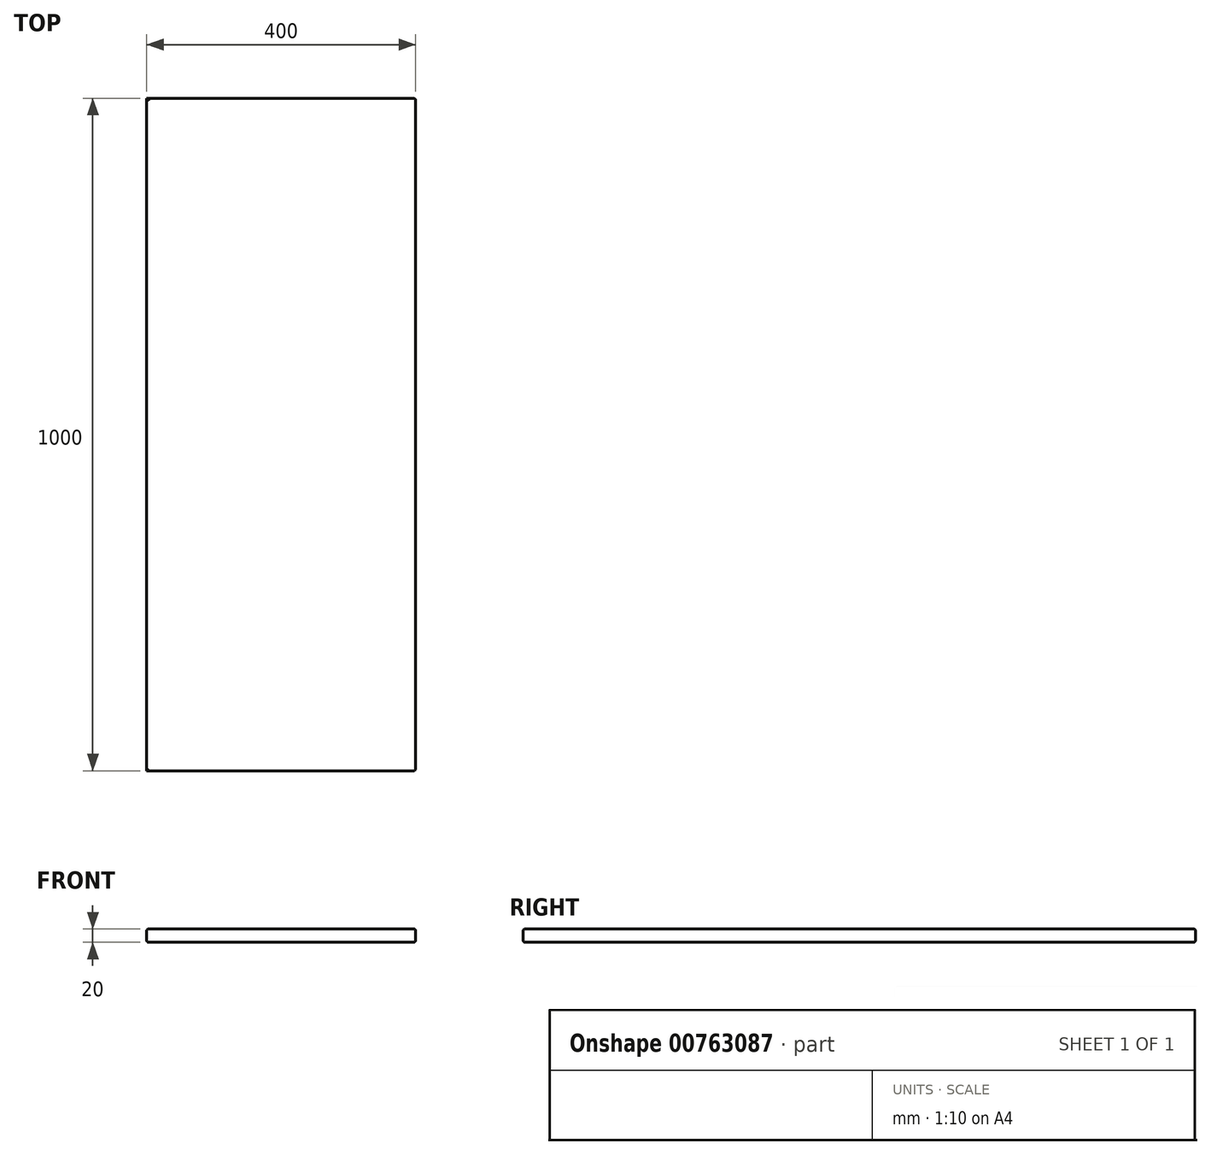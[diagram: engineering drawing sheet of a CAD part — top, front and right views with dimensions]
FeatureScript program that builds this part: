
annotation { "Feature Type Name" : "Feature", "Feature Type Description" : "" }
export const myFeature = defineFeature(function(context is Context, id is Id, definition is map)
    precondition{}
    {
        {
            var Q0;
            Q0=qCreatedBy(makeId("Front.planeOp"),FACE);
            var sketch = newSketch(context, id + "F0", { "sketchPlane" : qUnion([Q0])});
            skLineSegment(sketch, "E0.bottom", {"start": v(-233.94, 20.37) * mm, "end": v(166.06, 20.37) * mm});
            skLineSegment(sketch, "E0.top", {"start": v(-233.94, 0.37) * mm, "end": v(166.06, 0.37) * mm});
            skLineSegment(sketch, "E0.left", {"start": v(-233.94, 20.37) * mm, "end": v(-233.94, 0.37) * mm});
            skLineSegment(sketch, "E0.right", {"start": v(166.06, 20.37) * mm, "end": v(166.06, 0.37) * mm});
            skSolve(sketch);
        }
        {
            var Q0;
            Q0 = qSketchRegion(id + "F0", true);
            extrude(context, id + "F1", {"entities" : qUnion([Q0]), "depth" : 1000 * mm, "offsetDistance" : 25 * mm});
        }
        {
            var Q0;
            Q0=makeQuery(id+"F1.opExtrude","SWEPT_EDGE",EDGE,{"disambiguationData":[OSD([sQuery(id+"F0.wireOp",EDGE,"E0.bottom"),sQuery(id+"F0.wireOp",EDGE,"E0.right")])]});
            var Q1;
            Q1=makeQuery(id+"F1.opExtrude","SWEPT_EDGE",EDGE,{"disambiguationData":[OSD([sQuery(id+"F0.wireOp",EDGE,"E0.top"),sQuery(id+"F0.wireOp",EDGE,"E0.right")])]});
            fillet(context, id + "F2", {"entities" : qUnion([Q0, Q1]), "radius" : 3 * mm, "tangentPropagation" : true, "allowEdgeOverflow" : false});
        }
        {
            var Q0;
            Q0=makeQuery(id+"F1.opExtrude","CAP_EDGE",EDGE,{"disambiguationData":[OSD([sQuery(id+"F0.wireOp",EDGE,"E0.bottom")])],"isStart":true});
            var Q1;
            Q1=makeQuery(id+"F1.opExtrude","SWEPT_FACE",FACE,{"disambiguationData":[OSD([sQuery(id+"F0.wireOp",EDGE,"E0.bottom")])]});
            var Q2;
            Q2=makeQuery(id+"F1.opExtrude","SWEPT_FACE",FACE,{"disambiguationData":[OSD([sQuery(id+"F0.wireOp",EDGE,"E0.top")])]});
            fillet(context, id + "F3", {"entities" : qUnion([Q0, Q1, Q2]), "radius" : 3 * mm, "tangentPropagation" : true, "allowEdgeOverflow" : false});
        }
        {
            var Q0;
            Q0=makeQuery(id+"F1.opExtrude","CAP_FACE",FACE,{"disambiguationData":[OSD([sQuery(id+"F0.wireOp",EDGE,"E0.bottom"),sQuery(id+"F0.wireOp",EDGE,"E0.top"),sQuery(id+"F0.wireOp",EDGE,"E0.left"),sQuery(id+"F0.wireOp",EDGE,"E0.right")])],"isStart":false});
            var sketch = newSketch(context, id + "F4", { "sketchPlane" : qUnion([Q0])});
            skLineSegment(sketch, "E1", {"start": v(-233.94, 10.37) * mm, "end": v(163.06, 10.37) * mm, "construction": true});
            skLineSegment(sketch, "E2", {"start": v(-233.94, 10.37) * mm, "end": v(-133.94, 10.37) * mm, "construction": true});
            skLineSegment(sketch, "E3", {"start": v(163.06, 10.37) * mm, "end": v(63.06, 10.37) * mm, "construction": true});
            skSolve(sketch);
        }
        {
            var Q0;
            Q0=makeQuery(id+"F1.opExtrude","CAP_FACE",FACE,{"disambiguationData":[OSD([sQuery(id+"F0.wireOp",EDGE,"E0.bottom"),sQuery(id+"F0.wireOp",EDGE,"E0.top"),sQuery(id+"F0.wireOp",EDGE,"E0.left"),sQuery(id+"F0.wireOp",EDGE,"E0.right")])],"isStart":true});
            var sketch = newSketch(context, id + "F5", { "sketchPlane" : qUnion([Q0])});
            skLineSegment(sketch, "E4", {"start": v(-163.06, 10.37) * mm, "end": v(-63.06, 10.37) * mm, "construction": true});
            skLineSegment(sketch, "E5", {"start": v(233.94, 10.37) * mm, "end": v(133.94, 10.37) * mm, "construction": true});
            skSolve(sketch);
        }
    });
